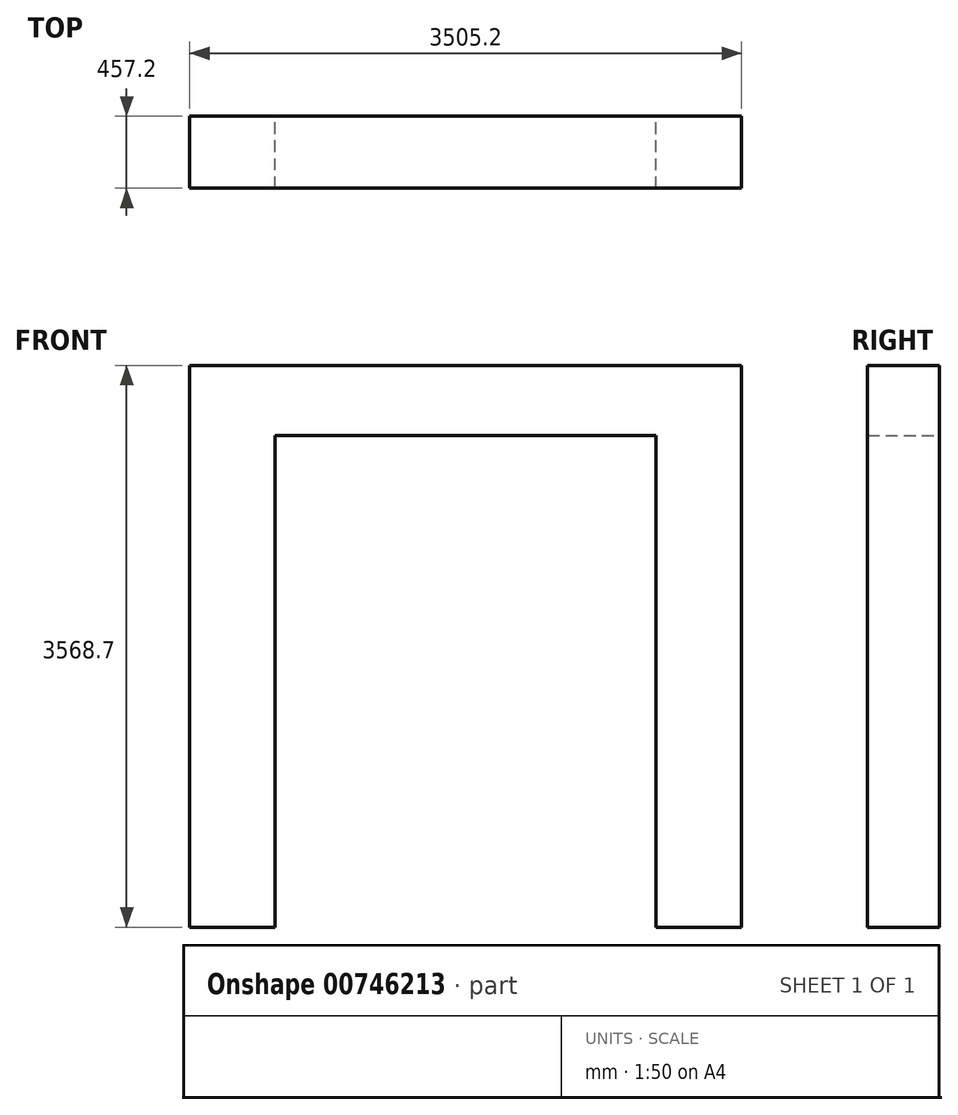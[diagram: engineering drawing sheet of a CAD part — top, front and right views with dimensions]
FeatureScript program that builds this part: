
annotation { "Feature Type Name" : "Feature", "Feature Type Description" : "" }
export const myFeature = defineFeature(function(context is Context, id is Id, definition is map)
    precondition{}
    {
        {
            var Q0;
            Q0=qCreatedBy(makeId("Front.planeOp"),FACE);
            var sketch = newSketch(context, id + "F0", { "sketchPlane" : qUnion([Q0])});
            skLineSegment(sketch, "E0.bottom", {"start": v(1752.6, 0) * mm, "end": v(1209.67, 0) * mm});
            skLineSegment(sketch, "E0.top", {"start": v(1752.6, 3568.7) * mm, "end": v(-1752.6, 3568.7) * mm});
            skLineSegment(sketch, "E0.left", {"start": v(1752.6, 0) * mm, "end": v(1752.6, 3568.7) * mm});
            skLineSegment(sketch, "E0.right", {"start": v(-1752.6, 0) * mm, "end": v(-1752.6, 3568.7) * mm});
            skPoint(sketch, "E0.middle", {"position": v(0, 1784.35) * mm});
            skLineSegment(sketch, "E1.bottom", {"start": v(1209.67, 3124.2) * mm, "end": v(-1209.67, 3124.2) * mm});
            skLineSegment(sketch, "E1.left", {"start": v(1209.68, 3124.2) * mm, "end": v(1209.67, 0) * mm});
            skLineSegment(sketch, "E1.right", {"start": v(-1209.67, 3124.2) * mm, "end": v(-1209.68, 0) * mm});
            skPoint(sketch, "E1.middle", {"position": v(0, 1562.1) * mm});
            skLineSegment(sketch, "E2.trimOffspring", {"start": v(-1209.68, 0) * mm, "end": v(-1752.6, 0) * mm});
            skSolve(sketch);
        }
        {
            var Q0;
            Q0 = qSketchRegion(id + "F0", true);
            extrude(context, id + "F1", {"entities" : qUnion([Q0]), "depth" : 457.2 * mm, "offsetDistance" : 25.4 * mm});
        }
    });
